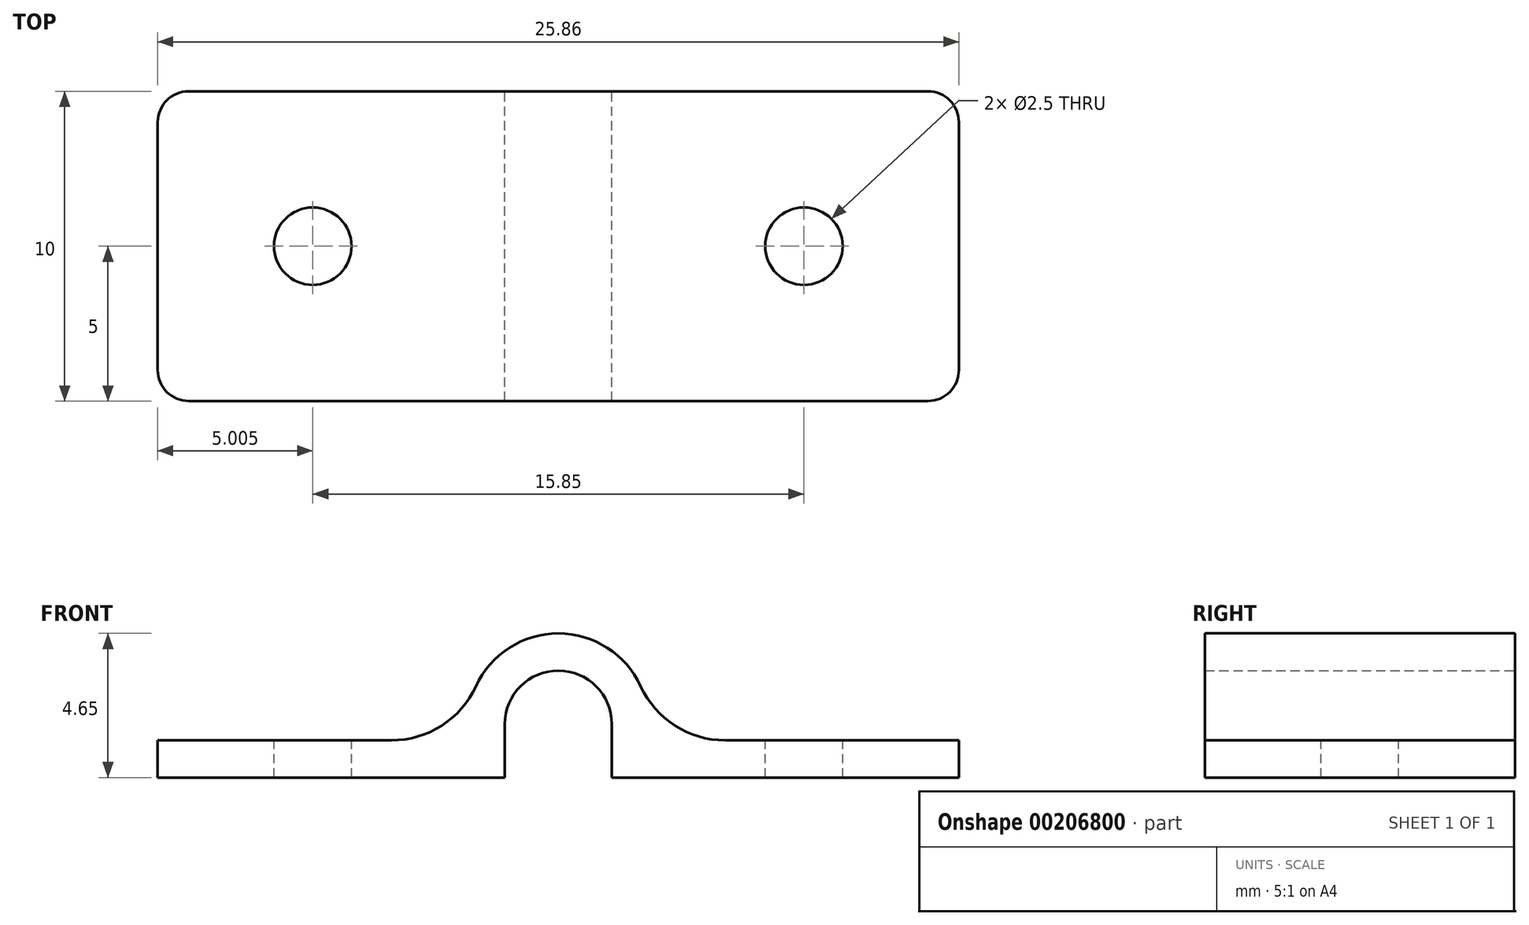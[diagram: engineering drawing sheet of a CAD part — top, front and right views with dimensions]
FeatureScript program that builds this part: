
annotation { "Feature Type Name" : "Feature", "Feature Type Description" : "" }
export const myFeature = defineFeature(function(context is Context, id is Id, definition is map)
    precondition{}
    {
        {
            var Q0;
            Q0=qCreatedBy(makeId("Front.planeOp"),FACE);
            var sketch = newSketch(context, id + "F0", { "sketchPlane" : qUnion([Q0])});
            skCircle(sketch, "E0", {"center": v(0, 1.72) * mm, "radius": 1.38 * mm, "construction": true});
            skArc(sketch, "E1.0", {"start": v(1.73, 1.72) * mm, "mid": v(0, 3.45) * mm, "end": v(-1.72, 1.73) * mm});
            skLineSegment(sketch, "E2", {"start": v(1.73, 1.72) * mm, "end": v(1.73, 0) * mm});
            skLineSegment(sketch, "E3", {"start": v(1.73, 0) * mm, "end": v(-1.73, 0) * mm});
            skLineSegment(sketch, "E4", {"start": v(-1.73, 0) * mm, "end": v(-1.72, 1.73) * mm});
            skLineSegment(sketch, "E5.0", {"start": v(2.93, 1.73) * mm, "end": v(2.93, 1.2) * mm});
            skArc(sketch, "E5.1", {"start": v(2.93, 1.73) * mm, "mid": v(0, 4.65) * mm, "end": v(-2.93, 1.73) * mm});
            skLineSegment(sketch, "E5.2", {"start": v(-2.93, 1.2) * mm, "end": v(-2.92, 1.73) * mm});
            skLineSegment(sketch, "E6", {"start": v(-2.93, 0) * mm, "end": v(-1.73, 0) * mm});
            skLineSegment(sketch, "E7", {"start": v(1.73, 0) * mm, "end": v(2.93, 0) * mm});
            skLineSegment(sketch, "E8", {"start": v(2.93, 1.2) * mm, "end": v(12.93, 1.2) * mm});
            skLineSegment(sketch, "E9", {"start": v(12.93, 1.2) * mm, "end": v(12.93, 0) * mm});
            skLineSegment(sketch, "E10", {"start": v(12.93, 0) * mm, "end": v(2.93, 0) * mm});
            skLineSegment(sketch, "E11.MirrorCS", {"start": v(-2.93, 1.2) * mm, "end": v(-12.93, 1.2) * mm});
            skLineSegment(sketch, "E12.MirrorCS", {"start": v(-12.93, 1.2) * mm, "end": v(-12.93, 0) * mm});
            skLineSegment(sketch, "E13.MirrorCS", {"start": v(-12.93, 0) * mm, "end": v(-2.93, 0) * mm});
            skSolve(sketch);
        }
        {
            var Q0;
            Q0=makeQuery(id+"F0.imprint","IMPRINT",FACE,{"disambiguationData":[TD([[makeQuery(id+"F0.imprint","IMPRINT",EDGE,{"derivedFrom":sQuery(id+"F0.wireOp",EDGE,"E1.0")}),-1.0]])]});
            extrude(context, id + "F1", {"entities" : qUnion([Q0]), "depth" : 10 * mm});
        }
        {
            var Q0;
            Q0=makeQuery(id+"F1.opExtrude","SWEPT_FACE",FACE,{"disambiguationData":[OSD([sQuery(id+"F0.wireOp",EDGE,"E8")])]});
            var sketch = newSketch(context, id + "F2", { "sketchPlane" : qUnion([Q0])});
            skLineSegment(sketch, "E14", {"start": v(2.93, 0) * mm, "end": v(12.93, -10) * mm, "construction": true});
            skCircle(sketch, "E15", {"center": v(7.93, -5) * mm, "radius": 1.25 * mm});
            skCircle(sketch, "E16.MirrorC", {"center": v(-7.92, -5) * mm, "radius": 1.25 * mm});
            skSolve(sketch);
        }
        {
            var Q0;
            Q0 = qSketchRegion(id + "F2", true);
            extrude(context, id + "F3", {"entities" : qUnion([Q0]), "operationType" : NewBodyOperationType.REMOVE, "endBound" : BoundingType.THROUGH_ALL, "oppositeDirection" : true, "depth" : 25 * mm});
        }
        {
            var Q0;
            Q0=makeQuery(id+"F1.opExtrude","CAP_EDGE",EDGE,{"disambiguationData":[OSD([sQuery(id+"F0.wireOp",EDGE,"E9")])],"isStart":false});
            var Q1;
            Q1=makeQuery(id+"F1.opExtrude","CAP_EDGE",EDGE,{"disambiguationData":[OSD([sQuery(id+"F0.wireOp",EDGE,"E12.MirrorCS")])],"isStart":false});
            var Q2;
            Q2=makeQuery(id+"F1.opExtrude","CAP_EDGE",EDGE,{"disambiguationData":[OSD([sQuery(id+"F0.wireOp",EDGE,"E9")])],"isStart":true});
            var Q3;
            Q3=makeQuery(id+"F1.opExtrude","CAP_EDGE",EDGE,{"disambiguationData":[OSD([sQuery(id+"F0.wireOp",EDGE,"E12.MirrorCS")])],"isStart":true});
            fillet(context, id + "F4", {"entities" : qUnion([Q0, Q1, Q2, Q3]), "radius" : 1 * mm, "tangentPropagation" : true, "allowEdgeOverflow" : false});
        }
        {
            var Q0;
            Q0=makeQuery(id+"F1.opExtrude","SWEPT_EDGE",EDGE,{"disambiguationData":[OSD([sQuery(id+"F0.wireOp",EDGE,"E5.0"),sQuery(id+"F0.wireOp",EDGE,"E8")])]});
            var Q1;
            Q1=makeQuery(id+"F1.opExtrude","SWEPT_EDGE",EDGE,{"disambiguationData":[OSD([sQuery(id+"F0.wireOp",EDGE,"E5.2"),sQuery(id+"F0.wireOp",EDGE,"E11.MirrorCS")])]});
            fillet(context, id + "F5", {"entities" : qUnion([Q0, Q1]), "radius" : 3 * mm, "tangentPropagation" : true, "allowEdgeOverflow" : false});
        }
    });
